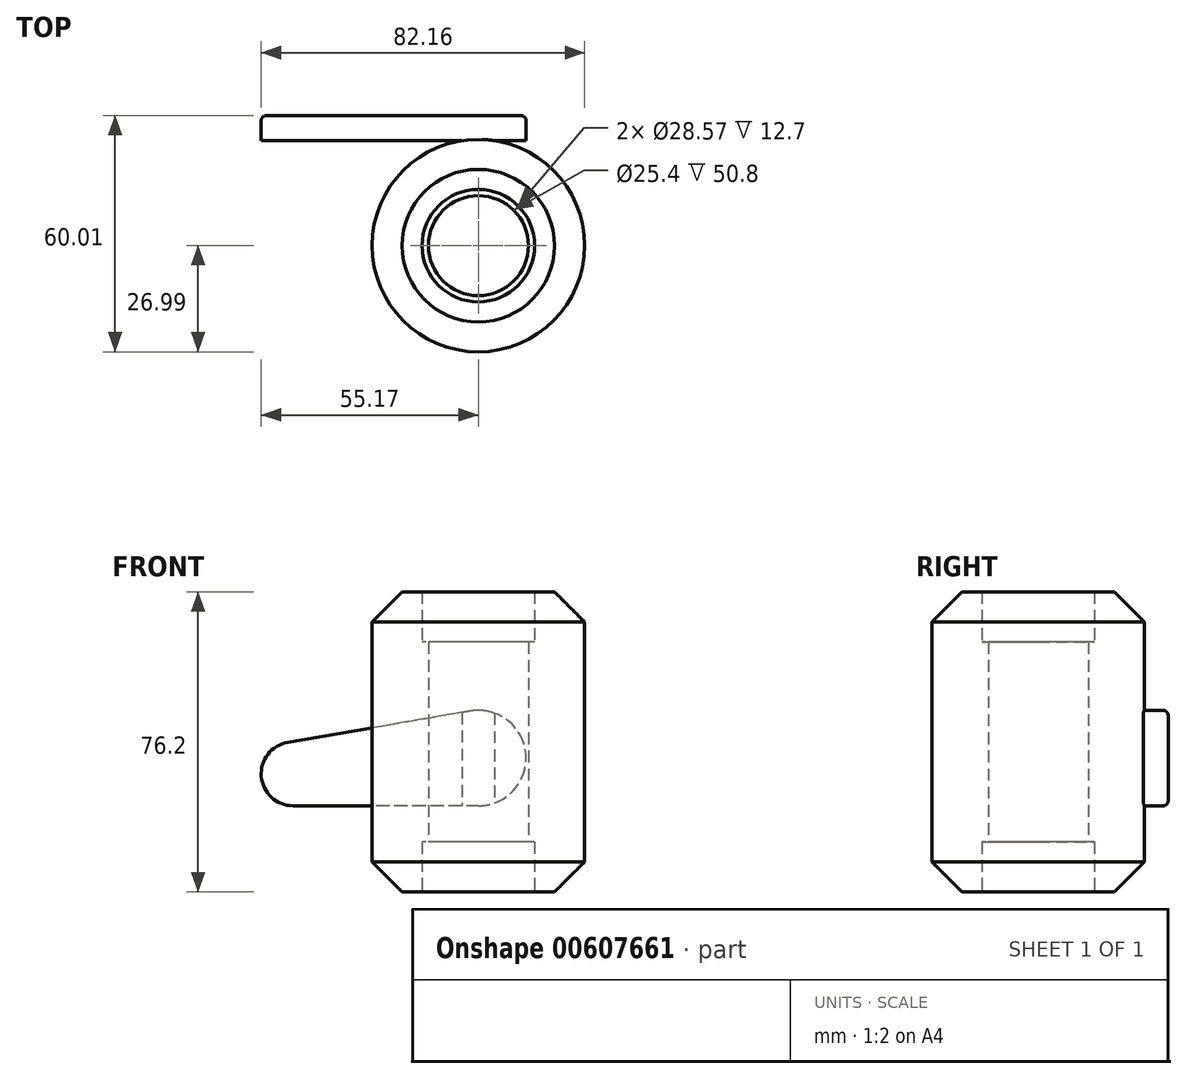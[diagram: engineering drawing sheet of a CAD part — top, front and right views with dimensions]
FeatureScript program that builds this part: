
annotation { "Feature Type Name" : "Feature", "Feature Type Description" : "" }
export const myFeature = defineFeature(function(context is Context, id is Id, definition is map)
    precondition{}
    {
        {
            var Q0;
            Q0=qCreatedBy(makeId("Top.planeOp"),FACE);
            var sketch = newSketch(context, id + "F0", { "sketchPlane" : qUnion([Q0])});
            skLineSegment(sketch, "E0", {"start": v(0, 0) * mm, "end": v(12.7, 0) * mm});
            skCircle(sketch, "E1", {"center": v(0, 0) * mm, "radius": 12.7 * mm});
            skCircle(sketch, "E2.0", {"center": v(0, 0) * mm, "radius": 14.29 * mm});
            skSolve(sketch);
        }
        {
            var Q0;
            Q0=qCreatedBy(makeId("Top.planeOp"),FACE);
            var sketch = newSketch(context, id + "F1", { "sketchPlane" : qUnion([Q0])});
            skSolve(sketch);
        }
        {
            var Q0;
            Q0=qSketchRegion(id+"F1",true);
            var Q1;
            Q1=makeQuery(id+"F0.imprint","IMPRINT",FACE,{"disambiguationData":[TD([[makeQuery(id+"F0.imprint","IMPRINT",EDGE,{"derivedFrom":sQuery(id+"F0.wireOp",EDGE,"E1")}),-1.0]])]});
            extrude(context, id + "F2", {"entities" : qUnion([Q0, Q1]), "depth" : 50.8 * mm, "offsetDistance" : 25.4 * mm});
        }
        {
            var Q0;
            Q0=qSketchRegion(id+"F0",true);
            var sketch = newSketch(context, id + "F3", { "sketchPlane" : qUnion([Q0])});
            skCircle(sketch, "E3.0", {"center": v(0, 0) * mm, "radius": 26.99 * mm});
            skSolve(sketch);
        }
        {
            var Q0;
            Q0=makeQuery(id+"F3.imprint","IMPRINT",FACE,{"disambiguationData":[TD([[makeQuery(id+"F3.imprint","IMPRINT",EDGE,{"derivedFrom":sQuery(id+"F3.wireOp",EDGE,"E3.0")}),1.0]])]});
            var Q1;
            Q1=sQuery(id+"F0.wireOp",EDGE,"E2.0");
            var Q2;
            Q2=sQuery(id+"F3.wireOp",EDGE,"E3.0");
            extrude(context, id + "F4", {"entities" : qUnion([Q0]), "operationType" : NewBodyOperationType.ADD, "surfaceEntities" : qUnion([Q1, Q2]), "depth" : 63.5 * mm, "offsetDistance" : 25.4 * mm, "hasSecondDirection" : true, "secondDirectionOppositeDirection" : true, "secondDirectionDepth" : 12.7 * mm});
        }
        {
            var Q0;
            Q0=makeQuery(id+"F4.opExtrude","CAP_EDGE",EDGE,{"disambiguationData":[OSD([sQuery(id+"F3.wireOp",EDGE,"E3.0")])],"isStart":false});
            var Q1;
            Q1=makeQuery(id+"F4.opExtrude","CAP_EDGE",EDGE,{"disambiguationData":[OSD([sQuery(id+"F3.wireOp",EDGE,"E3.0")])],"isStart":true});
            chamfer(context, id + "F5", {"entities" : qUnion([Q0, Q1]), "width" : 7.62 * mm, "tangentPropagation" : true});
        }
        {
            var Q0;
            Q0=qCreatedBy(makeId("Front.planeOp"),FACE);
            var sketch = newSketch(context, id + "F6", { "sketchPlane" : qUnion([Q0])});
            skCircle(sketch, "E4", {"center": v(0, 21.29) * mm, "radius": 12.12 * mm});
            skCircle(sketch, "E5", {"center": v(-47.06, 17.28) * mm, "radius": 8.1 * mm});
            skLineSegment(sketch, "E6", {"start": v(-2.05, 33.23) * mm, "end": v(-48.43, 25.27) * mm});
            skLineSegment(sketch, "E7", {"start": v(0, 9.17) * mm, "end": v(-47.06, 9.17) * mm});
            skSolve(sketch);
        }
        {
            var Q0;
            Q0 = qSketchRegion(id + "F6", true);
            extrude(context, id + "F7", {"entities" : qUnion([Q0]), "operationType" : NewBodyOperationType.ADD, "oppositeDirection" : true, "depth" : 33.02 * mm, "offsetDistance" : 25.4 * mm, "hasSecondDirection" : true, "secondDirectionOppositeDirection" : true, "secondDirectionDepth" : 26.67 * mm});
        }
        {
            var Q0;
            Q0=makeQuery(id+"F7.opExtrude","CAP_FACE",FACE,{"disambiguationData":[OSD([sQuery(id+"F6.wireOp",EDGE,"E4"),sQuery(id+"F6.wireOp",EDGE,"E5"),sQuery(id+"F6.wireOp",EDGE,"E6"),sQuery(id+"F6.wireOp",EDGE,"E7")])],"isStart":false});
            fillet(context, id + "F8", {"entities" : qUnion([Q0]), "radius" : 1.27 * mm, "tangentPropagation" : true, "allowEdgeOverflow" : false});
        }
    });
